# Revit family: xToilet_Tissue_Dispenser-Bobrick-TrimLineSeries-B-35883
name_source: partatom
category: Specialty Equipment
revit_build: Autodesk Revit 2014 (Build: 20130308_1515(x64)
units: mm (PartAtom-declared; Revit-internal decimal feet)

## types (1)
- B-35883
    ADA Compliant = Yes
    Assembly Code = E1090900
    Default Elevation = 25"
    Description = TrimLineSeries™ Recessed Multi-Roll Toilet Tissue Dispenser
    Height = 8 7/16"
    Installation Type = Recessed
    Length = 4 1/2"
    Manufacturer = Bobrick Washroom Equipment, Inc.
    Material = Stainless Steel-Bobrick-Type 304-Satin
    Model = B-35883
    Price = Prices may vary. Please consult Manufacturer Representative for most up-to-date price list.
    Product Documentation Link = http://bobrick.com
    Product Page URL = http://bobrick.com
    Specification = Recessed multi-roll toilet tissue dispenser shall be Type-304 stainless steel with all-welded construction; exposed surfaces shall have satin fi nish. Door shall be Type-304, 20-gauge (0.9mm) secured to cabinet with two rivets; and equipped with a tumbler lock keyed like other Bobrick washroom accessories. Spindle shall be Type-304, 18-gauge (1.2mm), 1" diameter (25mm) stainless steel. Theft resistant, removable with key provided.
    URL = http://bobrick.com
    Warranty Information = 1 Year Limited Warranty
    Width = 13 5/8"

## geometry (parser evidence)
native form markers: Sweep x2
no freeform markers — native parametric forms only
